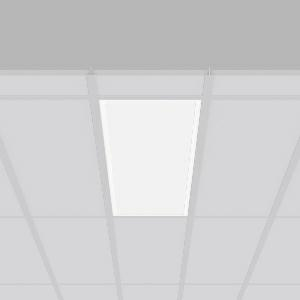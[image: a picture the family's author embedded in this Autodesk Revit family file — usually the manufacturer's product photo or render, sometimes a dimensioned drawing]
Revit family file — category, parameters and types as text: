
# Revit family: sidelite_eco_672370_002_89_a26e
name_source: partatom
category: Lighting Fixtures
units: mm (PartAtom-declared; Revit-internal decimal feet)

## family parameters
Cut with Voids When Loaded = No
Host = Face
Light Source = No
Part Type = Normal
Room Calculation Point = No
Round Connector Dimension = Use Diameter
Shared = No

## types (1)
- SIDELITE ECO (1 x LED Modul 830, 3300 lm, 3000)
    Apparent Load = 30 VA
    CIE Flux Codes = 46 79 96 100 100
    Color Rendering = 80
    Color Temperature = 3000
    Default Elevation = 1800 mm
    Description = Series: SIDELITE ECO
Highly economical recessed luminaire with progressive LED technology. For escape route illumination. Frame made of aluminium, powder-coated. Diffuser: plastic, opal. Lightguide and diffuser made of non-yellowing plastic (PMMA). Lateral light emission (RZB SIDELITE technology) for homogeneous light distribution. External driver. Second cable inlet for loop through. External driver with simple plug-in locking system. Extended connection cable (1.90 m). With AC Control monitoring module for LUXIFAIR central battery units. Luminaire can be used with accessories (to be ordered separately) for recessed, surface mounting or as pendant luminaire. 
Colour: white
Length: 1195 mm
Width: 295 mm
Cut-out length: 1170 mm
Cut-out width: 270 mm
Recess height: 160 mm
Luminaire: recess height: 40 mm
Weight: 3.94 kg
Operating mode: maintained power mode
Lamp: LED
Socket: without socket
Colour temperature: 3000K
Colour rendering index (CRI): 80
System power: 30 W
Rated luminous flux: 3300 lm
Luminous flux, emergency: 3300 lm
System power, emergency: 30 W
Control gear: Regulated power supply
Protection class: I
Type of protection: IP 20
    Height = 0 mm  [stored 0 ft]
    Lamp = 1 x LED Modul 830
    Lamp Light Flux = 3300 lm
    Lamp count = 1
    Length = 1195 mm
    Lifetime = 50000 h
    Luminous efficacy = 110 lm/W
    Manufacturer = RZB
    ModVariant = No
    Model = 672370.002.89
    Mounting Place = Ceiling
    Mounting Type = Recessed
    Number of Poles = 1
    OnlyDefault = Yes
    Power Factor = 1
    Product Name = SIDELITE ECO
    Product group = Recessed modular luminaires
    ProductGroupID = 406
    Protection Class = Protection class I
    Protection Degree = Degree of protection
    RLX_Detail_Level = 1
    RLX_Emergency_Light_Flux = 3300 lm
    RLX_Emergency_Type = 3
    RLX_Emergency_Type_DB = Yes
    RlxData = <blob elided: 31381 chars, md5=26134c85>
    Socket = socket
    Standby Power = 0 W
    System Light Flux = 3300 lm
    System Power = 30 W
    Type Comments = Product without accessories
    Type Image = 312365.002.jpg
    URL = http://relux.com
    VarID = ---
    Voltage = 0 V
    Weight = 0.00 kg
    Width = 295 mm

note: [stored X ft] marks values corroborated as IEEE doubles in the binary element streams (Revit-internal decimal feet)

## geometry (parser evidence)
native form markers: Blend x4, Sweep x11
no freeform markers — native parametric forms only
